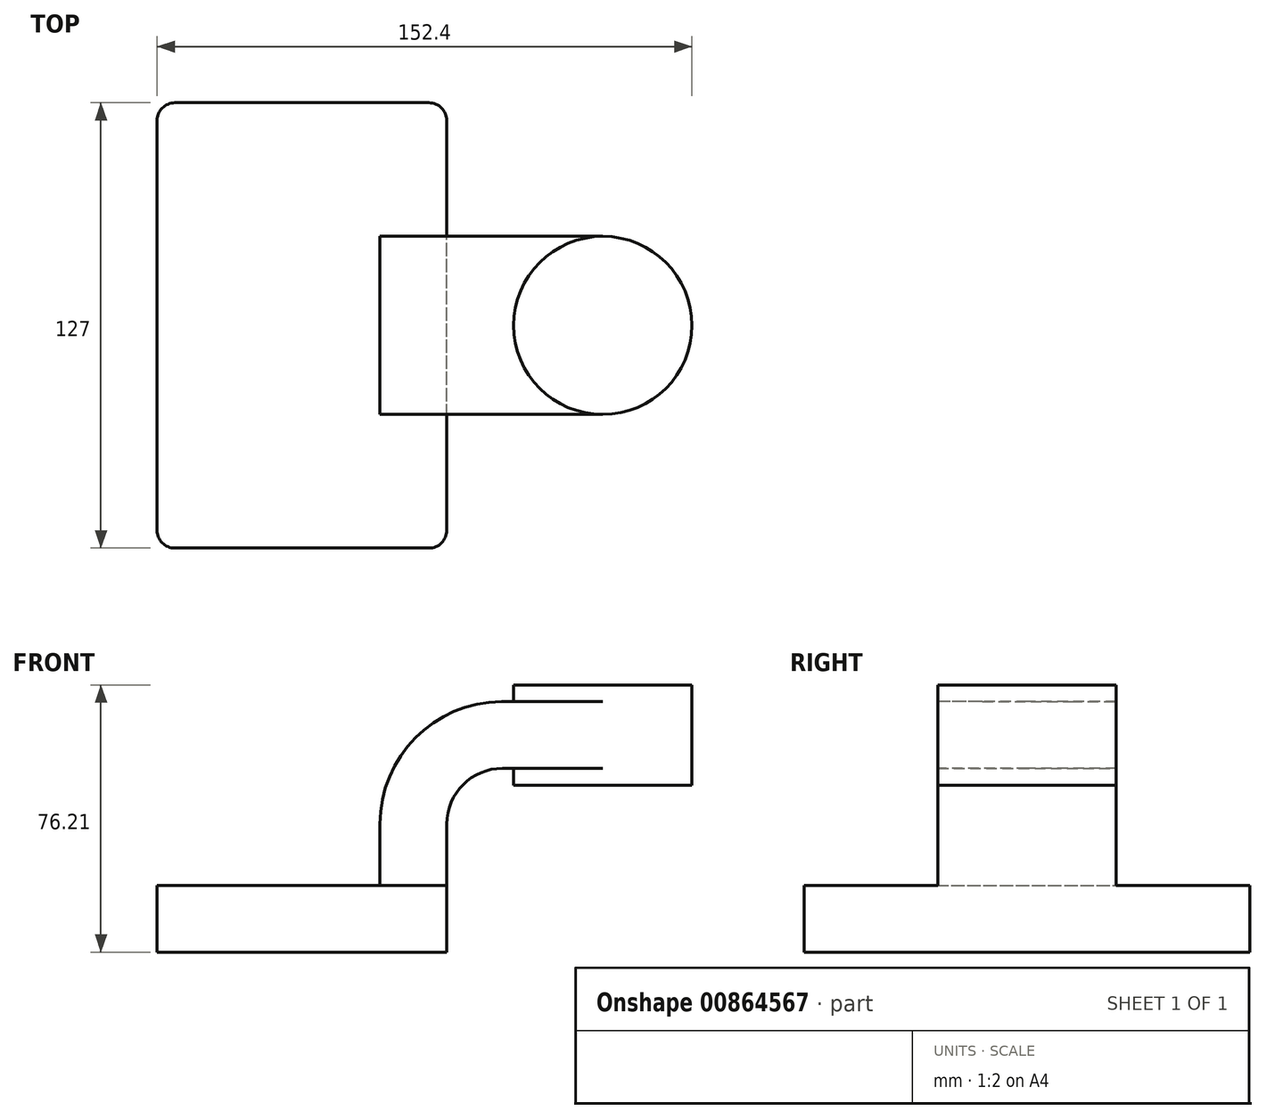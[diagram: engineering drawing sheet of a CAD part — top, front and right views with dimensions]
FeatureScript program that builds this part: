
annotation { "Feature Type Name" : "Feature", "Feature Type Description" : "" }
export const myFeature = defineFeature(function(context is Context, id is Id, definition is map)
    precondition{}
    {
        {
            var Q0;
            Q0=qCreatedBy(makeId("Front.planeOp"),FACE);
            var sketch = newSketch(context, id + "F0", { "sketchPlane" : qUnion([Q0])});
            skLineSegment(sketch, "E0.bottom", {"start": v(-41.28, 9.52) * mm, "end": v(41.27, 9.53) * mm});
            skLineSegment(sketch, "E0.top", {"start": v(-41.28, -9.53) * mm, "end": v(41.28, -9.53) * mm});
            skLineSegment(sketch, "E0.left", {"start": v(-41.28, 9.52) * mm, "end": v(-41.27, -9.53) * mm});
            skLineSegment(sketch, "E0.right", {"start": v(41.28, 9.53) * mm, "end": v(41.28, -9.52) * mm});
            skPoint(sketch, "E0.middle", {"position": v(0, 0) * mm});
            skLineSegment(sketch, "E1.bottom", {"start": v(60.33, 38.1) * mm, "end": v(111.12, 38.1) * mm});
            skLineSegment(sketch, "E1.top", {"start": v(60.32, 66.68) * mm, "end": v(111.12, 66.68) * mm});
            skLineSegment(sketch, "E1.left", {"start": v(60.33, 38.1) * mm, "end": v(60.32, 66.68) * mm});
            skLineSegment(sketch, "E1.right", {"start": v(111.12, 38.1) * mm, "end": v(111.12, 66.68) * mm});
            skPoint(sketch, "E1.middle", {"position": v(85.72, 52.39) * mm});
            skLineSegment(sketch, "E2", {"start": v(41.27, 9.53) * mm, "end": v(41.27, 27) * mm});
            skArc(sketch, "E3", {"start": v(41.27, 27) * mm, "mid": v(45.92, 38.23) * mm, "end": v(57.15, 42.88) * mm});
            skLineSegment(sketch, "E4", {"start": v(57.15, 42.88) * mm, "end": v(85.72, 42.88) * mm});
            skLineSegment(sketch, "E5", {"start": v(85.72, 38.1) * mm, "end": v(85.72, 66.68) * mm});
            skLineSegment(sketch, "E6.0", {"start": v(57.15, 61.93) * mm, "end": v(85.72, 61.93) * mm});
            skArc(sketch, "E6.1", {"start": v(22.22, 27) * mm, "mid": v(32.45, 51.7) * mm, "end": v(57.15, 61.93) * mm});
            skLineSegment(sketch, "E6.2", {"start": v(22.22, 9.53) * mm, "end": v(22.22, 27) * mm});
            skFitSpline(sketch, "E7", {"points": [v(-41.28, 9.53) * mm, v(57.15, 61.93) * mm], "startDerivative": vector(-0.33, 96.66) * mm, "endDerivative": vector(145.25, 0.55) * mm});
            skSolve(sketch);
        }
        {
            var Q0;
            Q0=makeQuery(id+"F0.imprint","IMPRINT",FACE,{"disambiguationData":[TD([[makeQuery(id+"F0.imprint","IMPRINT",EDGE,{"derivedFrom":sQuery(id+"F0.wireOp",EDGE,"E0.top")}),1.0]])]});
            extrude(context, id + "F1", {"entities" : qUnion([Q0]), "endBound" : BoundingType.SYMMETRIC, "depth" : 127 * mm, "offsetDistance" : 25.4 * mm});
        }
        {
            var Q0;
            {var subQ5=sQuery(id+"F0.wireOp",EDGE,"E2");Q0=makeQuery(id+"F0.imprint","IMPRINT",FACE,{"disambiguationData":[TD([[makeQuery(id+"F0.imprint","IMPRINT",EDGE,{"derivedFrom":subQ5}),1.0]])]});}
            var Q1;
            {var subQ0=sQuery(id+"F0.wireOp",EDGE,"E4");var subQ1=sQuery(id+"F0.wireOp",EDGE,"E1.left");var subQ2=makeQuery(id+"F0.imprint","INTERSECT",VERTEX,{"derivedFrom":[subQ1,subQ0]});Q1=makeQuery(id+"F0.imprint","IMPRINT",FACE,{"disambiguationData":[TD([[makeQuery(id+"F0.imprint","IMPRINT",EDGE,{"disambiguationData":[TD([[subQ2,-1.0]])],"derivedFrom":subQ1}),-1.0]])]});}
            extrude(context, id + "F2", {"entities" : qUnion([Q0, Q1]), "operationType" : NewBodyOperationType.ADD, "endBound" : BoundingType.SYMMETRIC, "depth" : 50.8 * mm, "offsetDistance" : 25.4 * mm});
        }
        {
            var Q0;
            {var subQ4=sQuery(id+"F0.wireOp",EDGE,"E6.1");Q0=makeQuery(id+"F0.imprint","IMPRINT",FACE,{"disambiguationData":[TD([[makeQuery(id+"F0.imprint","IMPRINT",EDGE,{"derivedFrom":subQ4}),1.0]])]});}
            extrude(context, id + "F3", {"entities" : qUnion([Q0]), "operationType" : NewBodyOperationType.ADD, "endBound" : BoundingType.SYMMETRIC, "depth" : 25.4 * mm, "offsetDistance" : 25.4 * mm});
        }
        {
            var Q0;
            {var subQ4=sQuery(id+"F0.wireOp",EDGE,"E1.right");Q0=makeQuery(id+"F0.imprint","IMPRINT",FACE,{"disambiguationData":[TD([[makeQuery(id+"F0.imprint","IMPRINT",EDGE,{"derivedFrom":subQ4}),1.0]])]});}
            var Q1;
            Q1=sQuery(id+"F0.wireOp",EDGE,"E5");
            revolve(context, id + "F4", {"operationType" : NewBodyOperationType.ADD, "surfaceOperationType" : NewSurfaceOperationType.NEW, "entities" : qUnion([Q0]), "axis" : qUnion([Q1]), "revolveType" : RevolveType.FULL});
        }
        {
            var Q0;
            Q0=makeQuery(id+"F1.opExtrude","CAP_EDGE",EDGE,{"disambiguationData":[OSD([sQuery(id+"F0.wireOp",EDGE,"E0.left")])],"isStart":false});
            var Q1;
            Q1=makeQuery(id+"F1.opExtrude","CAP_EDGE",EDGE,{"disambiguationData":[OSD([sQuery(id+"F0.wireOp",EDGE,"E0.right")])],"isStart":false});
            var Q2;
            Q2=makeQuery(id+"F1.opExtrude","CAP_EDGE",EDGE,{"disambiguationData":[OSD([sQuery(id+"F0.wireOp",EDGE,"E0.left")])],"isStart":true});
            var Q3;
            Q3=makeQuery(id+"F1.opExtrude","CAP_EDGE",EDGE,{"disambiguationData":[OSD([sQuery(id+"F0.wireOp",EDGE,"E0.right")])],"isStart":true});
            fillet(context, id + "F5", {"entities" : qUnion([Q0, Q1, Q2, Q3]), "radius" : 5.08 * mm, "tangentPropagation" : true, "allowEdgeOverflow" : false});
        }
    });
